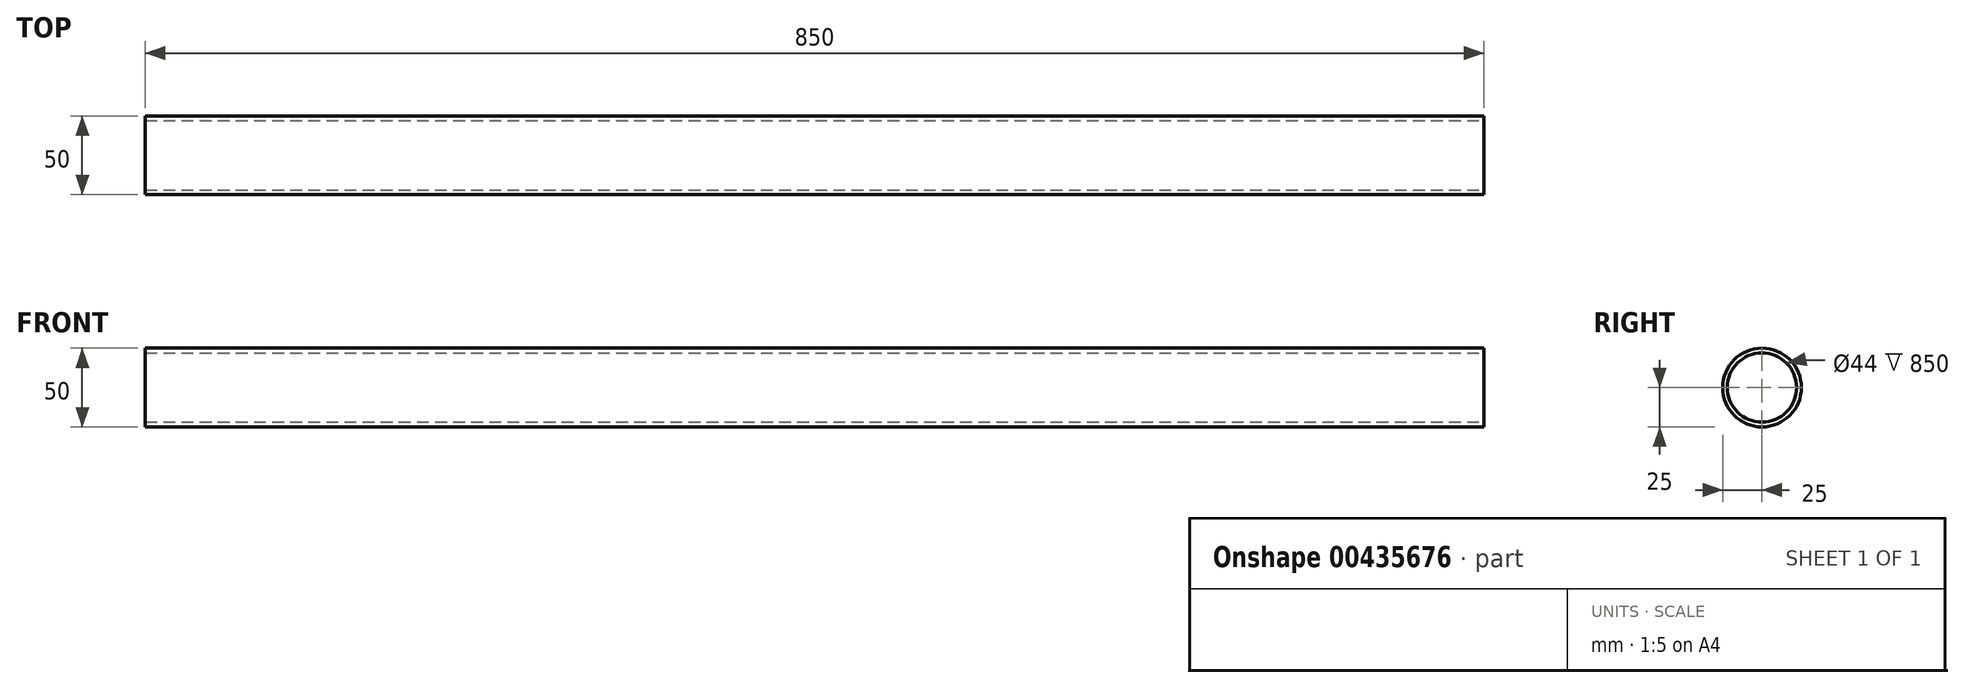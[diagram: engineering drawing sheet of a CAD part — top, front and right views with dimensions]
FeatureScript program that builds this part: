
annotation { "Feature Type Name" : "Feature", "Feature Type Description" : "" }
export const myFeature = defineFeature(function(context is Context, id is Id, definition is map)
    precondition{}
    {
        {
            var Q0;
            Q0=qCreatedBy(makeId("Top.planeOp"),FACE);
            var sketch = newSketch(context, id + "F0", { "sketchPlane" : qUnion([Q0])});
            skLineSegment(sketch, "E0", {"start": v(0, 0) * mm, "end": v(-403.1, 0) * mm});
            skLineSegment(sketch, "E1", {"start": v(-403.1, 0) * mm, "end": v(446.9, 0) * mm});
            skLineSegment(sketch, "E2.0.left", {"start": v(-403.1, 25) * mm, "end": v(446.9, 25) * mm});
            skLineSegment(sketch, "E2.0.right", {"start": v(-403.1, -25) * mm, "end": v(446.9, -25) * mm});
            skLineSegment(sketch, "E3", {"start": v(-403.1, 25) * mm, "end": v(-403.1, -25) * mm});
            skLineSegment(sketch, "E4", {"start": v(446.9, 25) * mm, "end": v(446.9, -25) * mm});
            skSolve(sketch);
        }
        {
            var Q0;
            Q0 = qSketchRegion(id + "F0", true);
            extrude(context, id + "F1", {"entities" : qUnion([Q0]), "endBound" : BoundingType.SYMMETRIC, "depth" : 50 * mm});
        }
        {
            var Q0;
            Q0=makeQuery(id+"F1.opExtrude","CAP_EDGE",EDGE,{"disambiguationData":[OSD([sQuery(id+"F0.wireOp",EDGE,"E2.0.right")])],"isStart":true});
            var Q1;
            Q1=makeQuery(id+"F1.opExtrude","CAP_EDGE",EDGE,{"disambiguationData":[OSD([sQuery(id+"F0.wireOp",EDGE,"E2.0.left")])],"isStart":true});
            var Q2;
            Q2=makeQuery(id+"F1.opExtrude","CAP_EDGE",EDGE,{"disambiguationData":[OSD([sQuery(id+"F0.wireOp",EDGE,"E2.0.left")])],"isStart":false});
            var Q3;
            Q3=makeQuery(id+"F1.opExtrude","CAP_EDGE",EDGE,{"disambiguationData":[OSD([sQuery(id+"F0.wireOp",EDGE,"E2.0.right")])],"isStart":false});
            fillet(context, id + "F2", {"entities" : qUnion([Q0, Q1, Q2, Q3]), "radius" : 25 * mm, "tangentPropagation" : true, "allowEdgeOverflow" : false});
        }
        {
            var Q0;
            Q0=qCreatedBy(makeId("Right.planeOp"),FACE);
            var sketch = newSketch(context, id + "F3", { "sketchPlane" : qUnion([Q0])});
            skCircle(sketch, "E5", {"center": v(0, 0) * mm, "radius": 22.07 * mm});
            skSolve(sketch);
        }
        {
            var Q0;
            Q0=sQuery(id+"F3.wireOp",VERTEX,"E5.center");
            var Q1;
            Q1=makeQuery(id+"F1.opExtrude","SWEPT_BODY",BODY,{"disambiguationData":[OSD([sQuery(id+"F0.wireOp",EDGE,"E2.0.left"),sQuery(id+"F0.wireOp",EDGE,"E2.0.right"),sQuery(id+"F0.wireOp",EDGE,"E3"),sQuery(id+"F0.wireOp",EDGE,"E4")])]});
            hole(context, id + "F4", {"style" : HoleStyle.SIMPLE, "endStyle" : HoleEndStyle.THROUGH, "holeDiameter" : 44 * mm, "isTappedThrough" : true, "tappedDepth" : 12 * mm, "tapClearance" : 3, "locations" : qUnion([Q0]), "scope" : qUnion([Q1])});
        }
        {
            var Q0;
            Q0=makeQuery(id+"F1.opExtrude","SWEPT_FACE",FACE,{"disambiguationData":[OSD([sQuery(id+"F0.wireOp",EDGE,"E4")])]});
            var sketch = newSketch(context, id + "F5", { "sketchPlane" : qUnion([Q0])});
            skCircle(sketch, "E6", {"center": v(0, 0) * mm, "radius": 19.08 * mm});
            skSolve(sketch);
        }
        {
            var Q0;
            Q0=sQuery(id+"F5.wireOp",VERTEX,"E6.center");
            var Q1;
            Q1=makeQuery(id+"F1.opExtrude","SWEPT_BODY",BODY,{"disambiguationData":[OSD([sQuery(id+"F0.wireOp",EDGE,"E2.0.left"),sQuery(id+"F0.wireOp",EDGE,"E2.0.right"),sQuery(id+"F0.wireOp",EDGE,"E3"),sQuery(id+"F0.wireOp",EDGE,"E4")])]});
            hole(context, id + "F6", {"style" : HoleStyle.SIMPLE, "endStyle" : HoleEndStyle.THROUGH, "holeDiameter" : 44 * mm, "isTappedThrough" : true, "tappedDepth" : 12 * mm, "tapClearance" : 3, "locations" : qUnion([Q0]), "scope" : qUnion([Q1])});
        }
    });
